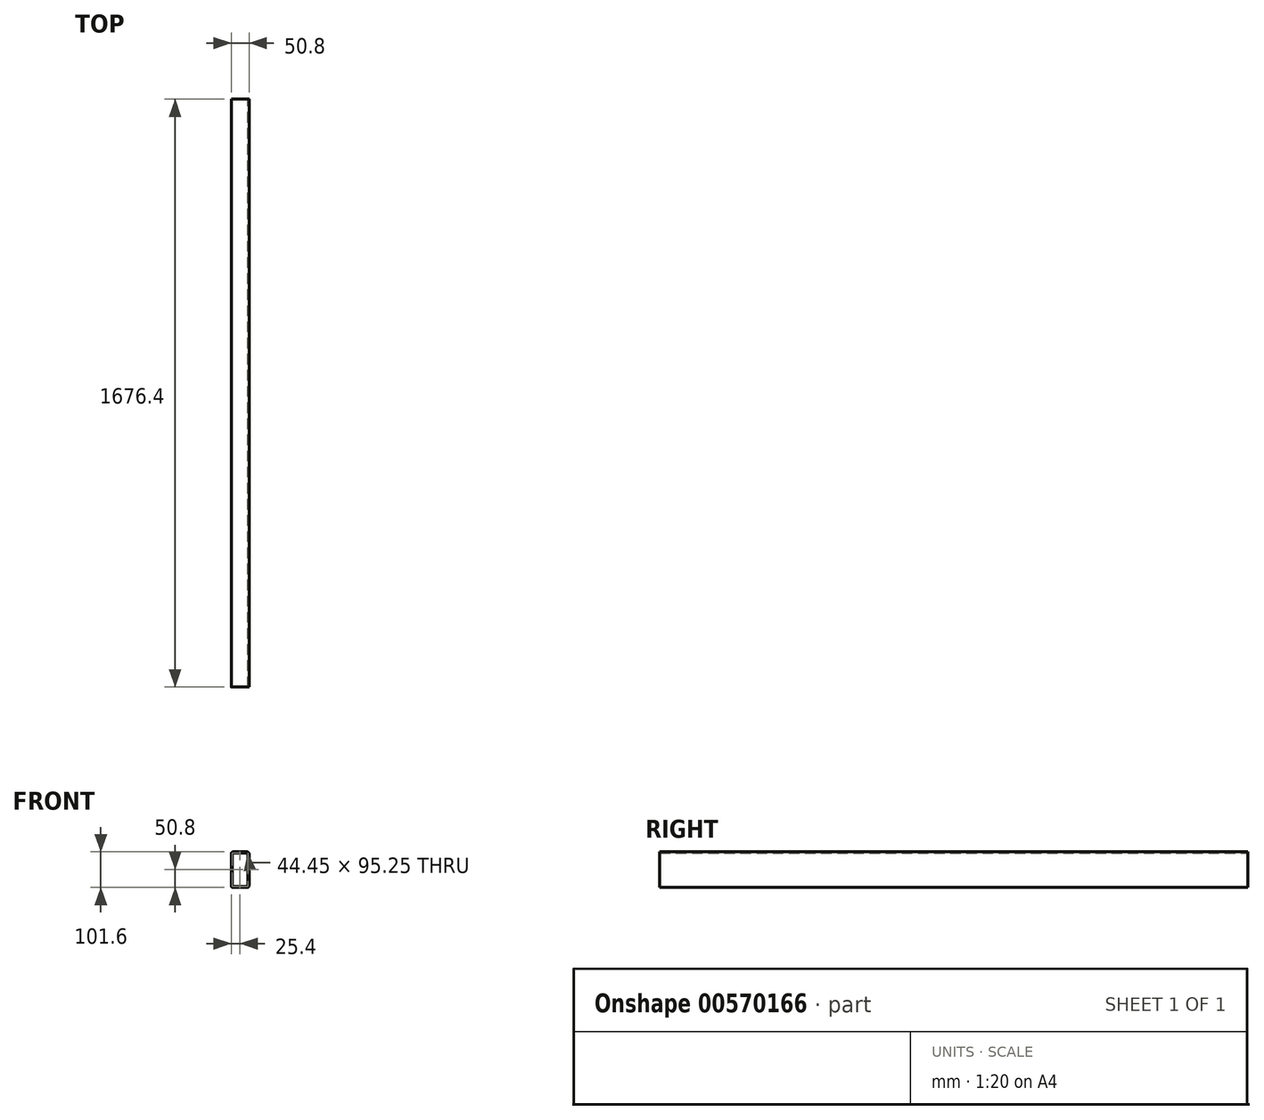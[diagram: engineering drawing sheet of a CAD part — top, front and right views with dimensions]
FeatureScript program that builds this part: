
annotation { "Feature Type Name" : "Feature", "Feature Type Description" : "" }
export const myFeature = defineFeature(function(context is Context, id is Id, definition is map)
    precondition{}
    {
        {
            var Q0;
            Q0=qCreatedBy(makeId("Front.planeOp"),FACE);
            var sketch = newSketch(context, id + "F0", { "sketchPlane" : qUnion([Q0])});
            skLineSegment(sketch, "E0.bottom", {"start": v(0, 0) * mm, "end": v(50.8, 0) * mm});
            skLineSegment(sketch, "E0.top", {"start": v(0, 101.6) * mm, "end": v(50.8, 101.6) * mm});
            skLineSegment(sketch, "E0.left", {"start": v(0, 0) * mm, "end": v(0, 101.6) * mm});
            skLineSegment(sketch, "E0.right", {"start": v(50.8, 0) * mm, "end": v(50.8, 101.6) * mm});
            skLineSegment(sketch, "E1.bottom", {"start": v(3.18, 3.17) * mm, "end": v(47.62, 3.17) * mm});
            skLineSegment(sketch, "E1.top", {"start": v(3.17, 98.43) * mm, "end": v(47.62, 98.43) * mm});
            skLineSegment(sketch, "E1.left", {"start": v(3.17, 3.18) * mm, "end": v(3.17, 98.43) * mm});
            skLineSegment(sketch, "E1.right", {"start": v(47.62, 3.18) * mm, "end": v(47.62, 98.43) * mm});
            skSolve(sketch);
        }
        {
            var Q0;
            Q0=makeQuery(id+"F0.imprint","IMPRINT",FACE,{"disambiguationData":[TD([[makeQuery(id+"F0.imprint","IMPRINT",EDGE,{"derivedFrom":sQuery(id+"F0.wireOp",EDGE,"E0.bottom")}),1.0]])]});
            extrude(context, id + "F1", {"entities" : qUnion([Q0]), "depth" : 1676.4 * mm, "offsetDistance" : 25.4 * mm});
        }
        {
            var Q0;
            Q0=makeQuery(id+"F1.opExtrude","SWEPT_EDGE",EDGE,{"disambiguationData":[OSD([sQuery(id+"F0.wireOp",EDGE,"E0.top"),sQuery(id+"F0.wireOp",EDGE,"E0.right")])]});
            var Q1;
            Q1=makeQuery(id+"F1.opExtrude","SWEPT_EDGE",EDGE,{"disambiguationData":[OSD([sQuery(id+"F0.wireOp",EDGE,"E0.bottom"),sQuery(id+"F0.wireOp",EDGE,"E0.right")])]});
            var Q2;
            Q2=makeQuery(id+"F1.opExtrude","SWEPT_EDGE",EDGE,{"disambiguationData":[OSD([sQuery(id+"F0.wireOp",EDGE,"E0.top"),sQuery(id+"F0.wireOp",EDGE,"E0.left")])]});
            var Q3;
            Q3=makeQuery(id+"F1.opExtrude","SWEPT_EDGE",EDGE,{"disambiguationData":[OSD([sQuery(id+"F0.wireOp",EDGE,"E0.bottom"),sQuery(id+"F0.wireOp",EDGE,"E0.left")])]});
            fillet(context, id + "F2", {"entities" : qUnion([Q0, Q1, Q2, Q3]), "radius" : 5.08 * mm, "tangentPropagation" : true, "allowEdgeOverflow" : false});
        }
    });
